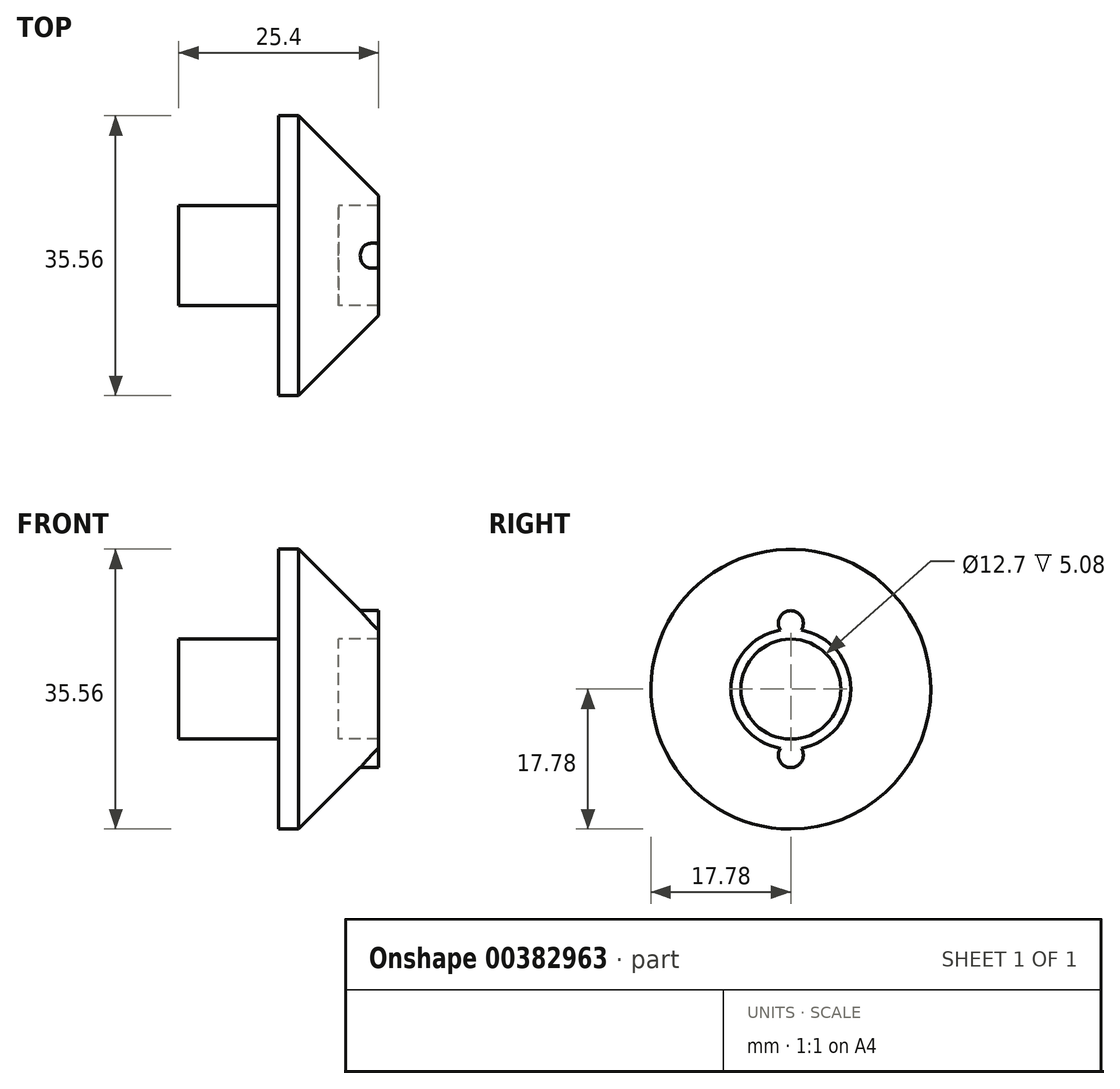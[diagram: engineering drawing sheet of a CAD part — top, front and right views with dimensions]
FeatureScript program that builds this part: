
annotation { "Feature Type Name" : "Feature", "Feature Type Description" : "" }
export const myFeature = defineFeature(function(context is Context, id is Id, definition is map)
    precondition{}
    {
        {
            var Q0;
            Q0=qCreatedBy(makeId("Right.planeOp"),FACE);
            var sketch = newSketch(context, id + "F0", { "sketchPlane" : qUnion([Q0])});
            skCircle(sketch, "E0", {"center": v(0, 0) * mm, "radius": 6.35 * mm});
            skCircle(sketch, "E1", {"center": v(0, 0) * mm, "radius": 17.78 * mm});
            skCircle(sketch, "E2", {"center": v(0, 8.38) * mm, "radius": 1.59 * mm});
            skCircle(sketch, "E3", {"center": v(0, -8.38) * mm, "radius": 1.59 * mm});
            skSolve(sketch);
        }
        {
            var Q0;
            Q0=makeQuery(id+"F0.imprint","IMPRINT",FACE,{"disambiguationData":[TD([[makeQuery(id+"F0.imprint","IMPRINT",EDGE,{"derivedFrom":sQuery(id+"F0.wireOp",EDGE,"E0")}),-1.0]])]});
            extrude(context, id + "F1", {"entities" : qUnion([Q0]), "depth" : 12.7 * mm});
        }
        {
            var Q0;
            Q0=makeQuery(id+"F1.opExtrude","CAP_EDGE",EDGE,{"disambiguationData":[OSD([sQuery(id+"F0.wireOp",EDGE,"E1")])],"isStart":false});
            chamfer(context, id + "F2", {"entities" : qUnion([Q0]), "width" : 10.16 * mm, "tangentPropagation" : true});
        }
        {
            var Q0;
            Q0=makeQuery(id+"F0.imprint","IMPRINT",FACE,{"disambiguationData":[TD([[makeQuery(id+"F0.imprint","IMPRINT",EDGE,{"derivedFrom":sQuery(id+"F0.wireOp",EDGE,"E0")}),1.0]])]});
            extrude(context, id + "F3", {"entities" : qUnion([Q0]), "operationType" : NewBodyOperationType.ADD, "depth" : 7.62 * mm});
        }
        {
            var Q0;
            Q0=makeQuery(id+"F0.imprint","IMPRINT",FACE,{"disambiguationData":[TD([[makeQuery(id+"F0.imprint","IMPRINT",EDGE,{"derivedFrom":sQuery(id+"F0.wireOp",EDGE,"E2")}),1.0]])]});
            var Q1;
            Q1=makeQuery(id+"F0.imprint","IMPRINT",FACE,{"disambiguationData":[TD([[makeQuery(id+"F0.imprint","IMPRINT",EDGE,{"derivedFrom":sQuery(id+"F0.wireOp",EDGE,"E3")}),1.0]])]});
            extrude(context, id + "F4", {"entities" : qUnion([Q0, Q1]), "operationType" : NewBodyOperationType.ADD, "depth" : 12.7 * mm});
        }
        {
            var Q0;
            Q0=makeQuery(id+"F0.imprint","IMPRINT",FACE,{"disambiguationData":[TD([[makeQuery(id+"F0.imprint","IMPRINT",EDGE,{"derivedFrom":sQuery(id+"F0.wireOp",EDGE,"E0")}),1.0]])]});
            extrude(context, id + "F5", {"entities" : qUnion([Q0]), "operationType" : NewBodyOperationType.ADD, "oppositeDirection" : true, "depth" : 12.7 * mm});
        }
    });
